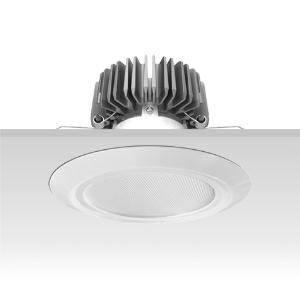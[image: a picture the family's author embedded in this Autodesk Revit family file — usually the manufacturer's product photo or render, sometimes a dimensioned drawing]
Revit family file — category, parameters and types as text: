
# Revit family: 3f_filippi_-_3f_reno_bianco_ampio_3f_filippi_-_30646_a01037_-_3f_reno_200_wh_2000-840_ep_wide___vs_wh_bc6c
name_source: partatom
category: Lighting Fixtures
units: mm (PartAtom-declared; Revit-internal decimal feet)

## family parameters
Cut with Voids When Loaded = No
Host = Face
Light Source = No
Part Type = Normal
Room Calculation Point = No
Round Connector Dimension = Use Diameter
Shared = No

## types (1)
- 3F Filippi - 3F Reno Bianco Ampio (1 x LED, 1723 lm, 21 W, 4000 K)
    Apparent Load = 21 VA
    Approval mark = ENEC
    CIE Flux Codes = 75 94 99 100 100
    Color Rendering = 80
    Color Temperature = 4000 K
    Control Gear = Electronic ballast
    Default Elevation = 1800 mm
    Description = ILLUMINOTECHNICAL
Luminous efficiency 100% (DLOR 100%, ULOR 0%).
Initial luminous flux of the luminaire 1723 lm.
Emergency luminaire luminous flux BLF 20%.
Direct symmetric wide distribution.
Installation Interdistance Transv.D = 1.16 x hu - Long.D = 1.14 x hu.
Average luminance <3000 cd/m² for radial angles >65°.
Tabular UGR (CIE 117 - 4H-8H; S=0.25H; 70/50/20): RUG 20.4 - 20.3.
Beam angle: 74° - 74°.
Luminous efficacy 82 lm/W.
Lifetime (L90/B10): 30000 h. (tq+25°C)
Lifetime (L85/B10): 50000 h. (tq+25°C)
Lifetime (L70/B10): 80000 h. (tq+25°C)
Sudden decreased luminous flux after 50000 hours: 0% (C0).
Photobiological safety in compliance with IEC/TR 62778: RG0 risk exempt, (IEC 62471).
In compliance with IEC/EN 62722-2-1 - IEC/EN 62717 standards.

SOURCE
Compact LED module 2000/840.
Energy efficiency class (UE 2019/2020 - UE 2019/2015): D.
CIE 13.3 Colour rendering index: CRI >80 (R9 <50%).
IES TM-30 Fidelity Index: Rf = 84 Rg = 95.
CCT nominal colour temperature 4000 K.
Colour initial tolerance (MacAdam): SDCM 3.
Zhaga Book 3 compliant.

MECHANICAL
Passive heat dissipator in die-casting aluminium, oversized, for optimum thermal management of the LED module.
Parabolic element with graduated/concentric rings in white polycarbonate.
Transparent external lens with glossy and satin differentiated surfaces, with a cooling and anti-insect system in methacrylate (PMMA).
Fastening spring clips in stainless steel.
Dimensions: diameter 226 mm, height 146 mm. Weight 1.63 kg.
IP44 protection degree for exposed part, IP20 for recessed part.
Mechanical strength to impacts IK06 (1 joule).
Glow-wire test resistance 650°C.

ELECTRICAL
Wiring on a separate unit.
Halogen Free electronic wiring 230V-50/60Hz, power factor 0.90, THD <25%, constant output current, SELV, class II, 1 driver.
Power of the luminaire 21 W.
CE - IEC 60598-1 - EN 60598-1.
EP maintained emergency wiring on board, 1h duration, 24h recharge; compliant with EN 60598-2-22, excluding high risk areas.
SAFE FLICKER: PstLM=<1 and SVM=<0.4 (IEC TR 61547-1 and IEC TR 63158), to ensure a more comfortable and safe light.
Ambient temperature from +5°C to +25°C.
Temperature class T6 max 85°C.
Relative humidity UR: <85%.

INSTALLATION
Pull-up recessed fitting.
False ceiling carving: 200 mm.
All accessories dedicated to this product are available on the Catalog and on our website www.3F-Filippi.com.

ACCESSORIES
A01037 - Anti-glare microprismatic VS moulded glass, tempered, not flammable, locked and in line with the trim, in white polycarbonate.

APPLICATIONS
Environments: architectural, commercial, exhibition areas, transit areas, corridors, shops, display windows, service areas.
In false ceilings with narrow voids.

WARNING
Luminaire designed for disposal/recycling at end-of-life.
Replaceable (LED only) light source by a professional. Replaceable control gear by a professional.
    Height = 0 mm  [stored 0 ft]
    Lamp = 1 x LED
    Lamp Light Flux = 1723 lm
    Lamp Power = 21 W
    Lamp count = 1
    Length = 226 mm
    Lifetime = 50000 h
    Luminous efficacy = 82 lm/W
    Manufacturer = 3F Filippi
    ModVariant = No
    Model = 3F Filippi - 30646+A01037 - 3F Reno 200 WH 2000-840 EP WIDE + VS WH
    Mounting Place = Ceiling
    Mounting Type = Recessed
    Number of Poles = 1
    OnlyDefault = Yes
    Power Factor = 1
    Product Name = 3F Filippi - 3F Reno Bianco Ampio
    Product group = recessed luminaire
    ProductGroupID = 4
    Protection Class = Protection class II
    Protection Degree = IP 20
    RLX_Detail_Level = 1
    RLX_Emergency_Light_Flux = 0 lm
    RLX_Emergency_Type = 0
    RLX_Emergency_Type_DB = No
    RlxData = <blob elided: 93789 chars, md5=ab5f11b4>
    Socket = socket
    Standby Power = 0 W
    System Light Flux = 1723 lm
    System Power = 21 W
    Type Comments = Product without accessories
    Type Image = 3ffilippi_3f_reno_200_wh_vs_smp.jpg
    URL = http://relux.com
    VarID = ---
    Voltage = 0 V
    Weight = 0.00 kg
    Width = 0 mm  [stored 0 ft]

note: [stored X ft] marks values corroborated as IEEE doubles in the binary element streams (Revit-internal decimal feet)

## geometry (parser evidence)
native form markers: Blend x4, Sweep x11
no freeform markers — native parametric forms only
